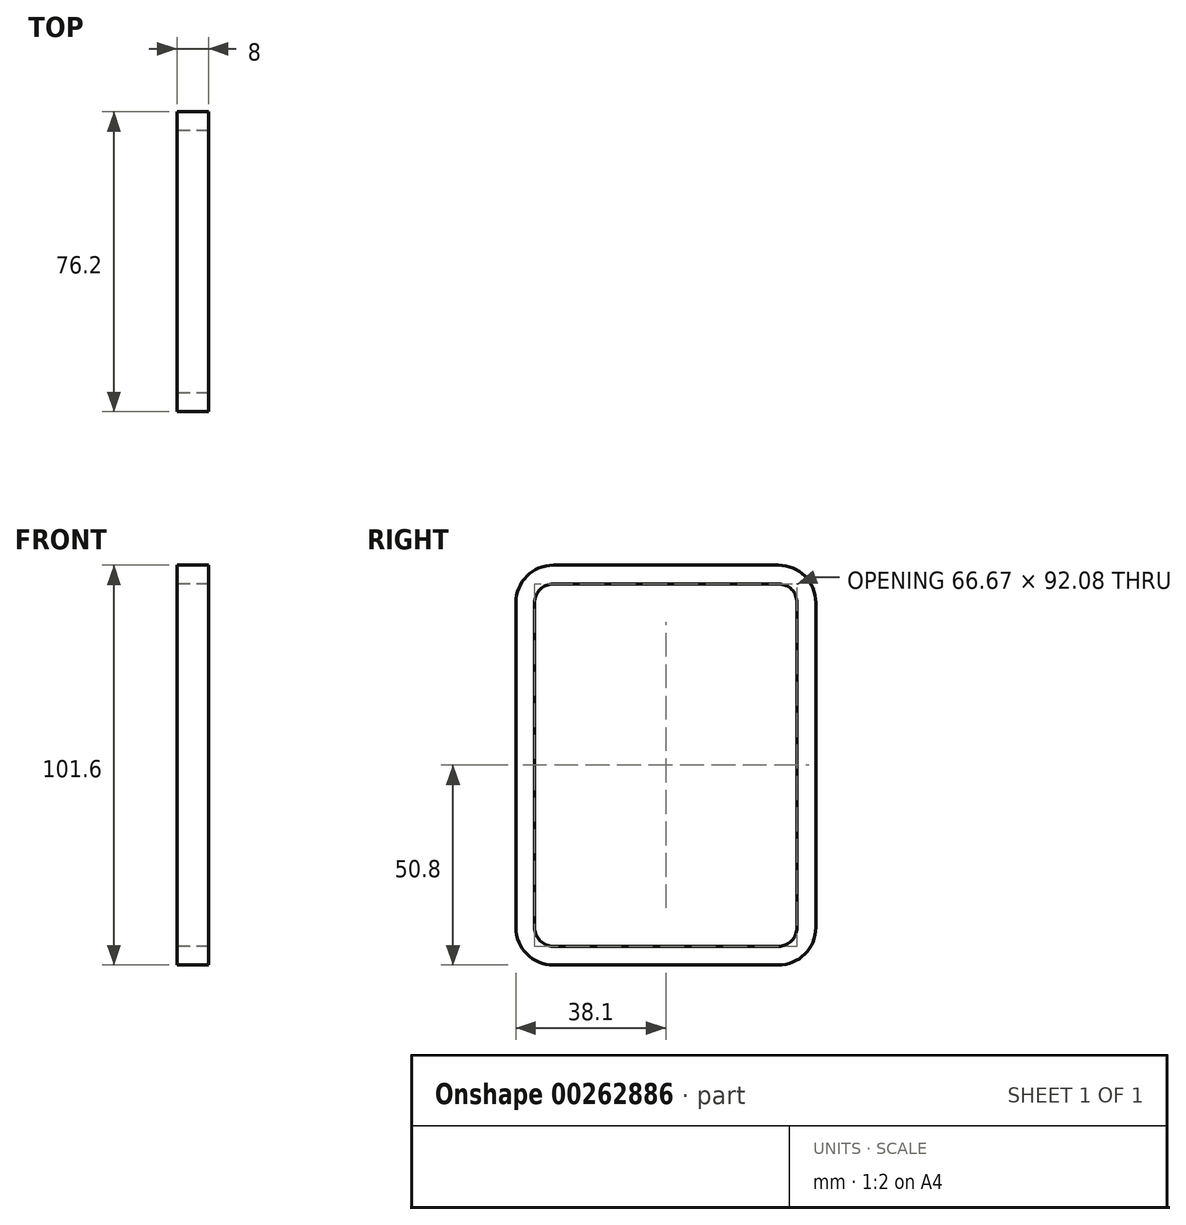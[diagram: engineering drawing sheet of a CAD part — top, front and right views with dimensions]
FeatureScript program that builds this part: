
annotation { "Feature Type Name" : "Feature", "Feature Type Description" : "" }
export const myFeature = defineFeature(function(context is Context, id is Id, definition is map)
    precondition{}
    {
        {
            assignVariable(context, id + "F0", {"name" : "Length", "anyValue" : 8});
        }
        {
            var Q0;
            Q0=qCreatedBy(makeId("Right.planeOp"),FACE);
            var sketch = newSketch(context, id + "F1", { "sketchPlane" : qUnion([Q0])});
            skLineSegment(sketch, "E0.bottom", {"start": v(-28.58, 50.8) * mm, "end": v(28.58, 50.8) * mm});
            skLineSegment(sketch, "E0.top", {"start": v(-28.58, -50.8) * mm, "end": v(28.58, -50.8) * mm});
            skLineSegment(sketch, "E0.left", {"start": v(-38.1, 41.28) * mm, "end": v(-38.1, -41.28) * mm});
            skLineSegment(sketch, "E0.right", {"start": v(38.1, 41.28) * mm, "end": v(38.1, -41.28) * mm});
            skPoint(sketch, "E0.middle", {"position": v(0, 0) * mm});
            skPoint(sketch, "E1.visualSharp", {"position": v(-38.1, 50.8) * mm});
            skArc(sketch, "E1.filletArc", {"start": v(-28.58, 50.8) * mm, "mid": v(-35.31, 48.01) * mm, "end": v(-38.1, 41.28) * mm});
            skPoint(sketch, "E2.visualSharp", {"position": v(-33.34, 46.04) * mm});
            skPoint(sketch, "E3.visualSharp", {"position": v(38.1, 50.8) * mm});
            skArc(sketch, "E3.filletArc", {"start": v(38.1, 41.28) * mm, "mid": v(35.31, 48.01) * mm, "end": v(28.58, 50.8) * mm});
            skPoint(sketch, "E4.visualSharp", {"position": v(33.34, 46.04) * mm});
            skPoint(sketch, "E5.visualSharp", {"position": v(33.34, -46.04) * mm});
            skPoint(sketch, "E6.visualSharp", {"position": v(-33.34, -46.04) * mm});
            skPoint(sketch, "E7.visualSharp", {"position": v(38.1, -50.8) * mm});
            skArc(sketch, "E7.filletArc", {"start": v(28.58, -50.8) * mm, "mid": v(35.31, -48.01) * mm, "end": v(38.1, -41.28) * mm});
            skPoint(sketch, "E8.visualSharp", {"position": v(-38.1, -50.8) * mm});
            skArc(sketch, "E8.filletArc", {"start": v(-38.1, -41.28) * mm, "mid": v(-35.31, -48.01) * mm, "end": v(-28.58, -50.8) * mm});
            skLineSegment(sketch, "E9.0", {"start": v(-28.57, 46.04) * mm, "end": v(28.58, 46.04) * mm});
            skArc(sketch, "E9.1", {"start": v(33.34, 41.28) * mm, "mid": v(31.94, 44.64) * mm, "end": v(28.58, 46.04) * mm});
            skArc(sketch, "E9.2", {"start": v(-28.57, 46.04) * mm, "mid": v(-31.94, 44.64) * mm, "end": v(-33.34, 41.28) * mm});
            skLineSegment(sketch, "E9.3", {"start": v(33.34, 41.28) * mm, "end": v(33.34, -41.28) * mm});
            skLineSegment(sketch, "E9.4", {"start": v(-33.34, 41.28) * mm, "end": v(-33.34, -41.28) * mm});
            skArc(sketch, "E9.5", {"start": v(-33.34, -41.28) * mm, "mid": v(-31.94, -44.64) * mm, "end": v(-28.58, -46.04) * mm});
            skLineSegment(sketch, "E9.6", {"start": v(-28.58, -46.04) * mm, "end": v(28.57, -46.04) * mm});
            skArc(sketch, "E9.7", {"start": v(28.57, -46.04) * mm, "mid": v(31.94, -44.64) * mm, "end": v(33.34, -41.28) * mm});
            skSolve(sketch);
        }
        {
            var Q0;
            Q0=makeQuery(id+"F1.imprint","IMPRINT",FACE,{"disambiguationData":[TD([[makeQuery(id+"F1.imprint","IMPRINT",EDGE,{"derivedFrom":sQuery(id+"F1.wireOp",EDGE,"E0.bottom")}),-1.0]])]});
            var Q1;
            Q1=sQuery(id+"F1.wireOp",EDGE,"E1.filletArc");
            var Q2;
            Q2=sQuery(id+"F1.wireOp",EDGE,"E0.left");
            var Q3;
            Q3=sQuery(id+"F1.wireOp",EDGE,"E0.bottom");
            var Q4;
            Q4=sQuery(id+"F1.wireOp",EDGE,"E3.filletArc");
            var Q5;
            Q5=sQuery(id+"F1.wireOp",EDGE,"E0.right");
            var Q6;
            Q6=sQuery(id+"F1.wireOp",EDGE,"E7.filletArc");
            var Q7;
            Q7=sQuery(id+"F1.wireOp",EDGE,"E0.top");
            var Q8;
            Q8=sQuery(id+"F1.wireOp",EDGE,"E8.filletArc");
            extrude(context, id + "F2", {"entities" : qUnion([Q0]), "surfaceEntities" : qUnion([Q1, Q2, Q3, Q4, Q5, Q6, Q7, Q8]), "endBound" : BoundingType.SYMMETRIC, "depth" : (getVariable(context, 'Length')) * mm, "hasSecondDirection" : true, "secondDirectionOppositeDirection" : true, "secondDirectionDepth" : 25.4 * mm});
        }
    });
